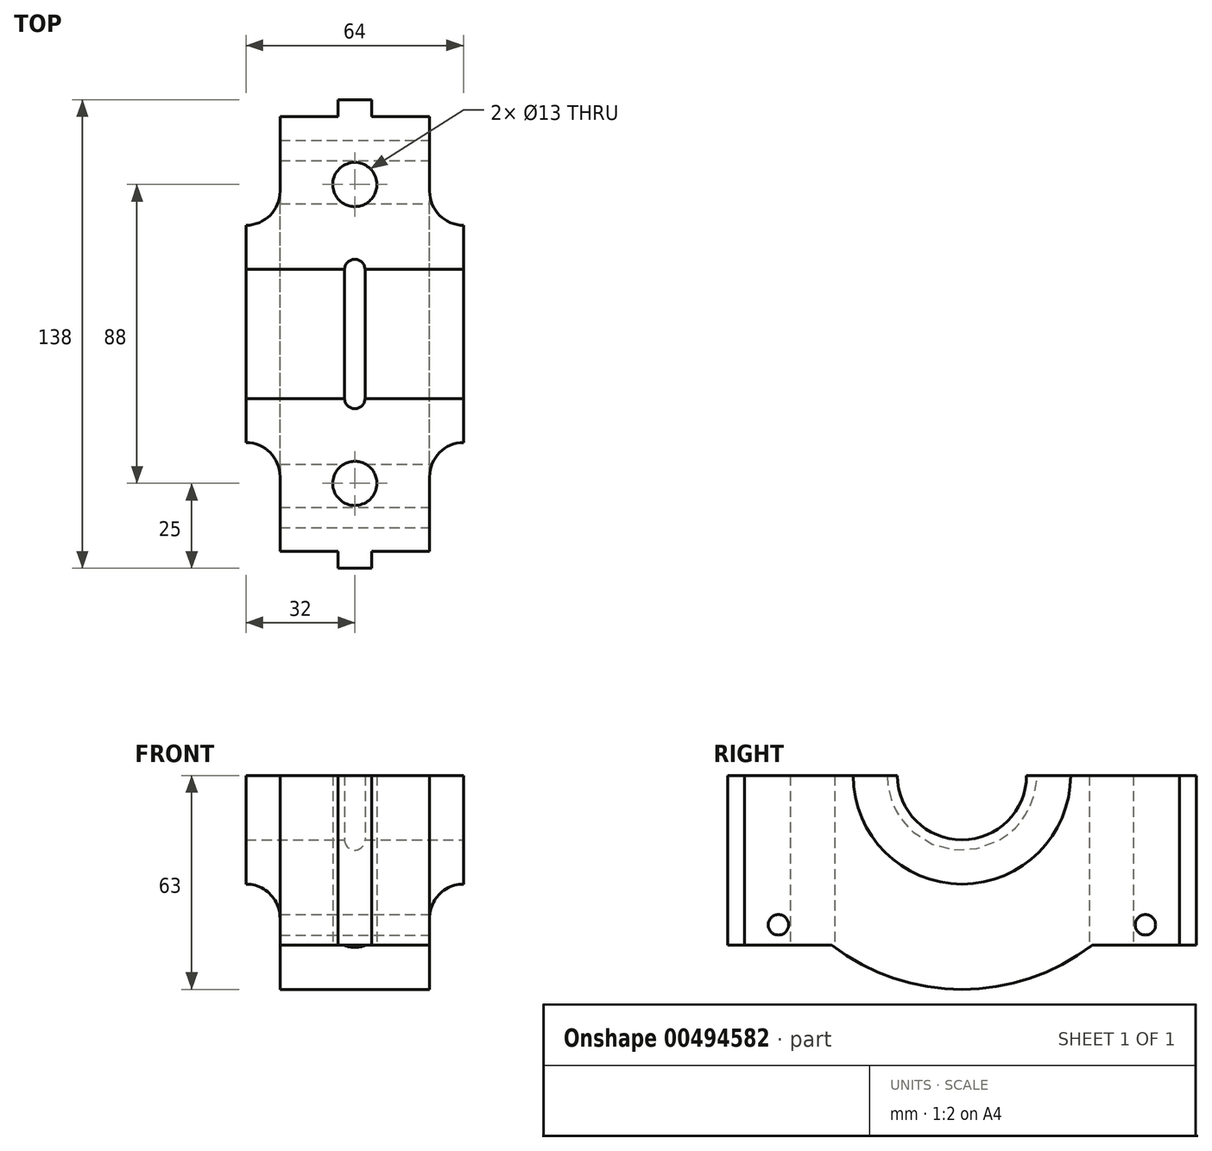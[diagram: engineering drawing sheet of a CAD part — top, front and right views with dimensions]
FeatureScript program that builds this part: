
annotation { "Feature Type Name" : "Feature", "Feature Type Description" : "" }
export const myFeature = defineFeature(function(context is Context, id is Id, definition is map)
    precondition{}
    {
        {
            var Q0;
            Q0=qCreatedBy(makeId("Top.planeOp"),FACE);
            var sketch = newSketch(context, id + "F0", { "sketchPlane" : qUnion([Q0])});
            skLineSegment(sketch, "E0.bottom", {"start": v(-22, 64) * mm, "end": v(-5, 64) * mm});
            skLineSegment(sketch, "E0.top", {"start": v(-22, -64) * mm, "end": v(-5, -64) * mm});
            skLineSegment(sketch, "E0.left", {"start": v(-22, 64) * mm, "end": v(-22, -64) * mm});
            skLineSegment(sketch, "E0.right", {"start": v(22, 64) * mm, "end": v(22, -64) * mm});
            skLineSegment(sketch, "E1.top", {"start": v(-5, -69) * mm, "end": v(5, -69) * mm});
            skLineSegment(sketch, "E1.left", {"start": v(-5, -64) * mm, "end": v(-5, -69) * mm});
            skLineSegment(sketch, "E1.right", {"start": v(5, -64) * mm, "end": v(5, -69) * mm});
            skLineSegment(sketch, "E2.top", {"start": v(-5, 69) * mm, "end": v(5, 69) * mm});
            skLineSegment(sketch, "E2.left", {"start": v(-5, 64) * mm, "end": v(-5, 69) * mm});
            skLineSegment(sketch, "E2.right", {"start": v(5, 64) * mm, "end": v(5, 69) * mm});
            skLineSegment(sketch, "E3.trimOffspring", {"start": v(5, 64) * mm, "end": v(22, 64) * mm});
            skLineSegment(sketch, "E4.trimOffspring", {"start": v(5, -64) * mm, "end": v(22, -64) * mm});
            skCircle(sketch, "E5", {"center": v(0, 44) * mm, "radius": 6.5 * mm});
            skCircle(sketch, "E6", {"center": v(0, -44) * mm, "radius": 6.5 * mm});
            skSolve(sketch);
        }
        {
            var Q0;
            Q0 = qSketchRegion(id + "F0", true);
            extrude(context, id + "F1", {"entities" : qUnion([Q0]), "depth" : 50 * mm, "offsetDistance" : 25 * mm});
        }
        {
            var Q0;
            Q0=makeQuery(id+"F1.opExtrude","SWEPT_FACE",FACE,{"disambiguationData":[OSD([sQuery(id+"F0.wireOp",EDGE,"E0.right")])]});
            var sketch = newSketch(context, id + "F2", { "sketchPlane" : qUnion([Q0])});
            skArc(sketch, "E7", {"start": v(-63, 50) * mm, "mid": v(0, -13) * mm, "end": v(63, 50) * mm});
            skLineSegment(sketch, "E8", {"start": v(-63, 50) * mm, "end": v(63, 50) * mm});
            skSolve(sketch);
        }
        {
            var Q0;
            Q0 = qSketchRegion(id + "F2", true);
            extrude(context, id + "F3", {"entities" : qUnion([Q0]), "operationType" : NewBodyOperationType.ADD, "oppositeDirection" : true, "depth" : 44 * mm, "offsetDistance" : 25 * mm});
        }
        {
            var Q0;
            Q0=makeQuery(id+"F3.boolean.opBoolean","MERGE",FACE,{"derivedFrom":[makeQuery(id+"F1.opExtrude","SWEPT_FACE",FACE,{"disambiguationData":[OSD([sQuery(id+"F0.wireOp",EDGE,"E0.right")])]}),makeQuery(id+"F3.opExtrude","CAP_FACE",FACE,{"disambiguationData":[OSD([sQuery(id+"F2.wireOp",EDGE,"E7"),sQuery(id+"F2.wireOp",EDGE,"E8")])],"isStart":true})]});
            var sketch = newSketch(context, id + "F4", { "sketchPlane" : qUnion([Q0])});
            skSolve(sketch);
        }
        {
            var Q0;
            Q0=qCreatedBy(makeId("Right.planeOp"),FACE);
            var sketch = newSketch(context, id + "F5", { "sketchPlane" : qUnion([Q0])});
            skArc(sketch, "E9", {"start": v(-32, 50) * mm, "mid": v(0, 18) * mm, "end": v(32, 50) * mm});
            skArc(sketch, "E10", {"start": v(-19, 50) * mm, "mid": v(0, 31) * mm, "end": v(19, 50) * mm});
            skLineSegment(sketch, "E11", {"start": v(0, 50) * mm, "end": v(-32, 50) * mm});
            skLineSegment(sketch, "E12", {"start": v(0, 50) * mm, "end": v(32, 50) * mm});
            skSolve(sketch);
        }
        {
            var Q0;
            Q0 = qSketchRegion(id + "F5", true);
            extrude(context, id + "F6", {"entities" : qUnion([Q0]), "operationType" : NewBodyOperationType.ADD, "endBound" : BoundingType.SYMMETRIC, "depth" : 64 * mm, "offsetDistance" : 25 * mm});
        }
        {
            var Q0;
            Q0=qCreatedBy(makeId("Right.planeOp"),FACE);
            var sketch = newSketch(context, id + "F7", { "sketchPlane" : qUnion([Q0])});
            skArc(sketch, "E13", {"start": v(-19, 50) * mm, "mid": v(0, 31) * mm, "end": v(19, 50) * mm});
            skLineSegment(sketch, "E14", {"start": v(0, 50) * mm, "end": v(-19, 50) * mm});
            skLineSegment(sketch, "E15", {"start": v(0, 50) * mm, "end": v(19, 50) * mm});
            skSolve(sketch);
        }
        {
            var Q0;
            Q0 = qSketchRegion(id + "F7", true);
            extrude(context, id + "F8", {"entities" : qUnion([Q0]), "operationType" : NewBodyOperationType.REMOVE, "endBound" : BoundingType.SYMMETRIC, "oppositeDirection" : true, "depth" : 100 * mm, "offsetDistance" : 25 * mm});
        }
        {
            var Q0;
            Q0=makeQuery(id+"F6.boolean.opBoolean","INTERSECT",EDGE,{"derivedFrom":[makeQuery(id+"F3.boolean.opBoolean","MERGE",FACE,{"derivedFrom":[makeQuery(id+"F1.opExtrude","SWEPT_FACE",FACE,{"disambiguationData":[OSD([sQuery(id+"F0.wireOp",EDGE,"E0.right")])]}),makeQuery(id+"F3.opExtrude","CAP_FACE",FACE,{"disambiguationData":[OSD([sQuery(id+"F2.wireOp",EDGE,"E7"),sQuery(id+"F2.wireOp",EDGE,"E8")])],"isStart":true})]}),makeQuery(id+"F6.opExtrude","SWEPT_FACE",FACE,{"disambiguationData":[OSD([sQuery(id+"F5.wireOp",EDGE,"E9")])]})]});
            var Q1;
            Q1=makeQuery(id+"F6.boolean.opBoolean","INTERSECT",EDGE,{"derivedFrom":[makeQuery(id+"F3.boolean.opBoolean","MERGE",FACE,{"derivedFrom":[makeQuery(id+"F1.opExtrude","SWEPT_FACE",FACE,{"disambiguationData":[OSD([sQuery(id+"F0.wireOp",EDGE,"E0.left")])]}),makeQuery(id+"F3.opExtrude","CAP_FACE",FACE,{"disambiguationData":[OSD([sQuery(id+"F2.wireOp",EDGE,"E7"),sQuery(id+"F2.wireOp",EDGE,"E8")])],"isStart":false})]}),makeQuery(id+"F6.opExtrude","SWEPT_FACE",FACE,{"disambiguationData":[OSD([sQuery(id+"F5.wireOp",EDGE,"E9")])]})]});
            fillet(context, id + "F9", {"entities" : qUnion([Q0, Q1]), "radius" : 10 * mm, "tangentPropagation" : true, "allowEdgeOverflow" : false});
        }
        {
            var Q0;
            {var subQ0=sQuery(id+"F2.wireOp",EDGE,"E8");var subQ2=sQuery(id+"F0.wireOp",EDGE,"E0.right");var subQ3=sQuery(id+"F0.wireOp",EDGE,"E4.trimOffspring");var subQ4=sQuery(id+"F5.wireOp",EDGE,"E12");var subQ5=sQuery(id+"F5.wireOp",EDGE,"E11");var subQ7=sQuery(id+"F0.wireOp",EDGE,"E1.right");var subQ8=sQuery(id+"F0.wireOp",EDGE,"E1.left");var subQ9=sQuery(id+"F0.wireOp",EDGE,"E1.top");var subQ10=sQuery(id+"F0.wireOp",EDGE,"E0.top");var subQ11=sQuery(id+"F0.wireOp",EDGE,"E0.left");Q0=makeQuery(id+"F8.boolean.opBoolean","SPLIT",FACE,{"disambiguationData":[TD([makeQuery(id+"F1.opExtrude","SWEPT_FACE",FACE,{"disambiguationData":[OSD([subQ10])]})])],"derivedFrom":makeQuery(id+"F6.boolean.opBoolean","MERGE",FACE,{"derivedFrom":[makeQuery(id+"F3.boolean.opBoolean","MERGE",FACE,{"derivedFrom":[makeQuery(id+"F1.opExtrude","CAP_FACE",FACE,{"disambiguationData":[OSD([sQuery(id+"F0.wireOp",EDGE,"E0.bottom"),subQ10,subQ11,subQ2,subQ9,subQ8,subQ7,sQuery(id+"F0.wireOp",EDGE,"E2.top"),sQuery(id+"F0.wireOp",EDGE,"E2.left"),sQuery(id+"F0.wireOp",EDGE,"E2.right"),sQuery(id+"F0.wireOp",EDGE,"E3.trimOffspring"),subQ3,sQuery(id+"F0.wireOp",EDGE,"E5"),sQuery(id+"F0.wireOp",EDGE,"E6")])],"isStart":false}),makeQuery(id+"F3.opExtrude","SWEPT_FACE",FACE,{"disambiguationData":[OSD([subQ0])]})]}),makeQuery(id+"F6.opExtrude","SWEPT_FACE",FACE,{"disambiguationData":[OSD([subQ5,subQ4])]})]})});}
            var sketch = newSketch(context, id + "F10", { "sketchPlane" : qUnion([Q0])});
            skCircle(sketch, "E16", {"center": v(0, -44) * mm, "radius": 6.5 * mm});
            skCircle(sketch, "E17", {"center": v(0, 44) * mm, "radius": 6.5 * mm});
            skSolve(sketch);
        }
        {
            var Q0;
            Q0 = qSketchRegion(id + "F10", true);
            extrude(context, id + "F11", {"entities" : qUnion([Q0]), "operationType" : NewBodyOperationType.REMOVE, "oppositeDirection" : true, "depth" : 100 * mm, "offsetDistance" : 25 * mm});
        }
        {
            var Q0;
            {var subQ1=sQuery(id+"F0.wireOp",EDGE,"E3.trimOffspring");var subQ2=sQuery(id+"F2.wireOp",EDGE,"E8");var subQ4=sQuery(id+"F0.wireOp",EDGE,"E0.right");var subQ5=sQuery(id+"F0.wireOp",EDGE,"E2.left");var subQ6=sQuery(id+"F0.wireOp",EDGE,"E2.right");var subQ7=sQuery(id+"F0.wireOp",EDGE,"E0.bottom");var subQ8=sQuery(id+"F0.wireOp",EDGE,"E0.left");var subQ9=sQuery(id+"F0.wireOp",EDGE,"E2.top");var subQ10=sQuery(id+"F5.wireOp",EDGE,"E12");var subQ11=sQuery(id+"F5.wireOp",EDGE,"E11");Q0=makeQuery(id+"F8.boolean.opBoolean","SPLIT",FACE,{"disambiguationData":[TD([makeQuery(id+"F1.opExtrude","SWEPT_FACE",FACE,{"disambiguationData":[OSD([subQ7])]})])],"derivedFrom":makeQuery(id+"F6.boolean.opBoolean","MERGE",FACE,{"derivedFrom":[makeQuery(id+"F3.boolean.opBoolean","MERGE",FACE,{"derivedFrom":[makeQuery(id+"F1.opExtrude","CAP_FACE",FACE,{"disambiguationData":[OSD([subQ7,sQuery(id+"F0.wireOp",EDGE,"E0.top"),subQ8,subQ4,sQuery(id+"F0.wireOp",EDGE,"E1.top"),sQuery(id+"F0.wireOp",EDGE,"E1.left"),sQuery(id+"F0.wireOp",EDGE,"E1.right"),subQ9,subQ5,subQ6,subQ1,sQuery(id+"F0.wireOp",EDGE,"E4.trimOffspring"),sQuery(id+"F0.wireOp",EDGE,"E5"),sQuery(id+"F0.wireOp",EDGE,"E6")])],"isStart":false}),makeQuery(id+"F3.opExtrude","SWEPT_FACE",FACE,{"disambiguationData":[OSD([subQ2])]})]}),makeQuery(id+"F6.opExtrude","SWEPT_FACE",FACE,{"disambiguationData":[OSD([subQ11,subQ10])]})]})});}
            var sketch = newSketch(context, id + "F12", { "sketchPlane" : qUnion([Q0])});
            skCircle(sketch, "E18", {"center": v(0, 19) * mm, "radius": 3 * mm});
            skSolve(sketch);
        }
        {
            var Q0;
            {var subQ12=sQuery(id+"F0.wireOp",EDGE,"E0.bottom");Q0=makeQuery(id+"F12.imprint","IMPRINT",FACE,{"disambiguationData":[TD([[makeQuery(id+"F12.imprint","IMPRINT",EDGE,{"derivedFrom":makeQuery(id+"F1.opExtrude","CAP_EDGE",EDGE,{"disambiguationData":[OSD([subQ12])],"isStart":false})}),-1.0]])]});}
            var sketch = newSketch(context, id + "F13", { "sketchPlane" : qUnion([Q0])});
            skLineSegment(sketch, "E19", {"start": v(0, 0) * mm, "end": v(21.04, 0) * mm});
            skSolve(sketch);
        }
        {
            var Q0;
            {var subQ0=sQuery(id+"F12.wireOp",EDGE,"E18");var subQ1=makeQuery(id+"F8.boolean.opBoolean","COPY",EDGE,{"derivedFrom":makeQuery(id+"F8.opExtrude","SWEPT_EDGE",EDGE,{"disambiguationData":[OSD([sQuery(id+"F7.wireOp",EDGE,"E13"),sQuery(id+"F7.wireOp",EDGE,"E15")])]})});var subQ2=makeQuery(id+"F12.imprint","INTERSECT",VERTEX,{"disambiguationData":[OD(0.0)],"derivedFrom":[subQ1,subQ0]});Q0=makeQuery(id+"F12.imprint","IMPRINT",FACE,{"disambiguationData":[TD([[makeQuery(id+"F12.imprint","IMPRINT",EDGE,{"disambiguationData":[TD([[subQ2,1.0]])],"derivedFrom":subQ0}),1.0]])]});}
            var Q1;
            Q1=sQuery(id+"F13.wireOp",EDGE,"E19");
            revolve(context, id + "F14", {"operationType" : NewBodyOperationType.REMOVE, "entities" : qUnion([Q0]), "axis" : qUnion([Q1]), "revolveType" : RevolveType.FULL, "oppositeDirection" : true});
        }
        {
            var Q0;
            {var subQ1=sQuery(id+"F0.wireOp",EDGE,"E0.right");Q0=makeQuery(id+"F4.imprint","IMPRINT",FACE,{"disambiguationData":[TD([[makeQuery(id+"F4.imprint","IMPRINT",EDGE,{"derivedFrom":makeQuery(id+"F1.opExtrude","CAP_EDGE",EDGE,{"disambiguationData":[OSD([subQ1])],"isStart":false})}),1.0]])]});}
            var sketch = newSketch(context, id + "F15", { "sketchPlane" : qUnion([Q0])});
            skCircle(sketch, "E20", {"center": v(-54, 6) * mm, "radius": 3 * mm});
            skCircle(sketch, "E21", {"center": v(54, 6) * mm, "radius": 3 * mm});
            skSolve(sketch);
        }
        {
            var Q0;
            Q0 = qSketchRegion(id + "F15", true);
            extrude(context, id + "F16", {"entities" : qUnion([Q0]), "operationType" : NewBodyOperationType.REMOVE, "oppositeDirection" : true, "depth" : 1000 * mm, "offsetDistance" : 25 * mm});
        }
    });
